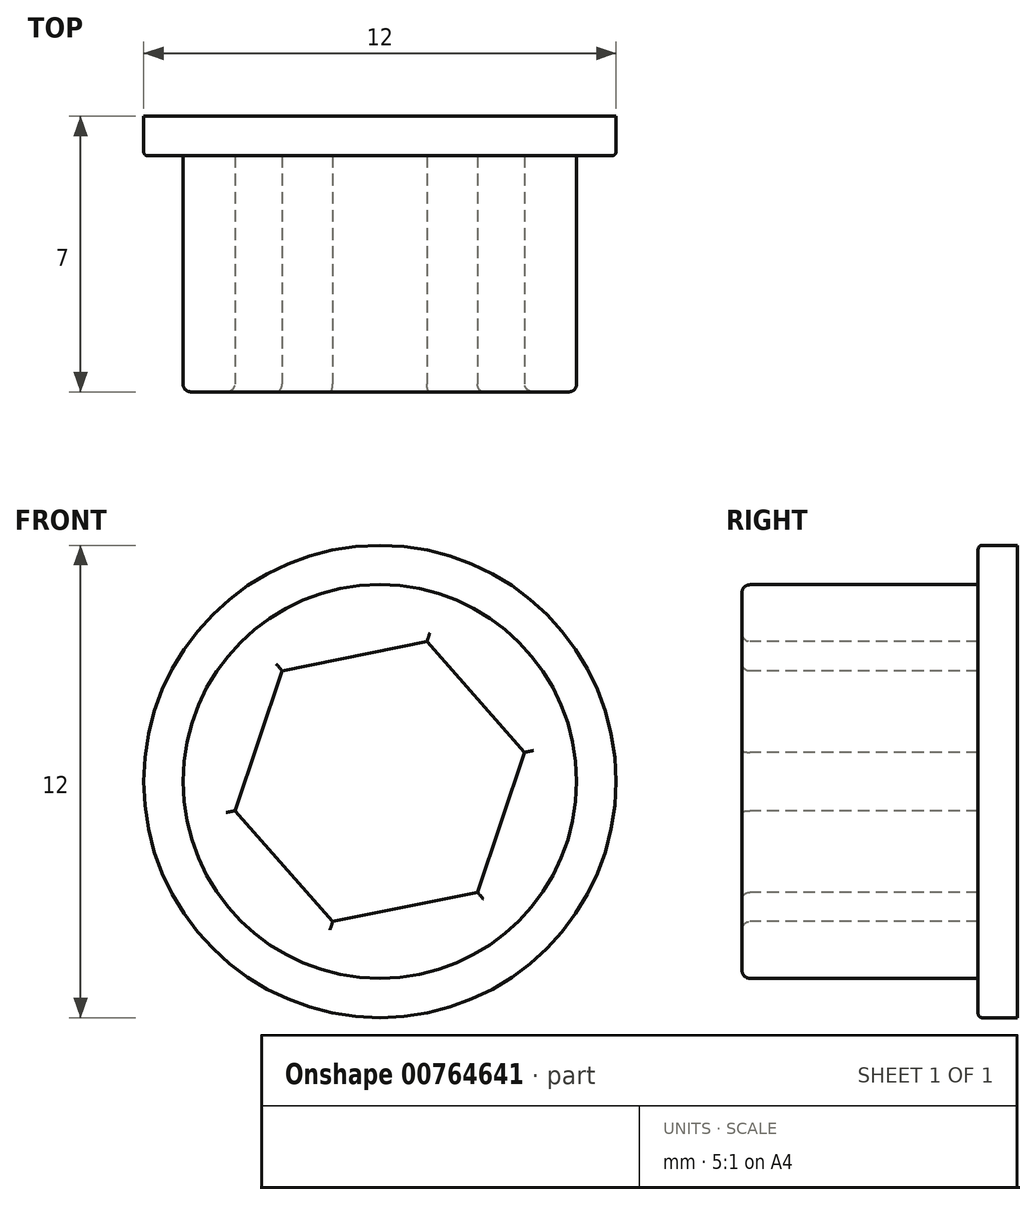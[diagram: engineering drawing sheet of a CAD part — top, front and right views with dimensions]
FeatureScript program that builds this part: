
annotation { "Feature Type Name" : "Feature", "Feature Type Description" : "" }
export const myFeature = defineFeature(function(context is Context, id is Id, definition is map)
    precondition{}
    {
        {
            var Q0;
            Q0=qCreatedBy(makeId("Front.planeOp"),FACE);
            var sketch = newSketch(context, id + "F0", { "sketchPlane" : qUnion([Q0])});
            skCircle(sketch, "E0", {"center": v(0, 0) * mm, "radius": 6 * mm});
            skSolve(sketch);
        }
        {
            var Q0;
            Q0 = qSketchRegion(id + "F0", true);
            extrude(context, id + "F1", {"entities" : qUnion([Q0]), "oppositeDirection" : true, "depth" : 1 * mm, "offsetDistance" : 25 * mm});
        }
        {
            var Q0;
            Q0=makeQuery(id+"F1.opExtrude","CAP_FACE",FACE,{"disambiguationData":[OSD([sQuery(id+"F0.wireOp",EDGE,"E0")])],"isStart":true});
            var sketch = newSketch(context, id + "F2", { "sketchPlane" : qUnion([Q0])});
            skCircle(sketch, "E1", {"center": v(0, 0) * mm, "radius": 5 * mm});
            skSolve(sketch);
        }
        {
            var Q0;
            Q0 = qSketchRegion(id + "F2", true);
            extrude(context, id + "F3", {"entities" : qUnion([Q0]), "operationType" : NewBodyOperationType.ADD, "depth" : 6 * mm, "offsetDistance" : 25 * mm});
        }
        {
            var Q0;
            Q0=makeQuery(id+"F3.opExtrude","CAP_FACE",FACE,{"disambiguationData":[OSD([sQuery(id+"F2.wireOp",EDGE,"E1")])],"isStart":false});
            var sketch = newSketch(context, id + "F4", { "sketchPlane" : qUnion([Q0])});
            skCircle(sketch, "E2.cCircle", {"center": v(0, 0) * mm, "radius": 3.25 * mm, "construction": true});
            skLineSegment(sketch, "E2.0", {"start": v(1.2, 3.56) * mm, "end": v(3.68, 0.74) * mm});
            skLineSegment(sketch, "E2.1", {"start": v(3.68, 0.74) * mm, "end": v(2.48, -2.81) * mm});
            skLineSegment(sketch, "E2.2", {"start": v(2.48, -2.81) * mm, "end": v(-1.2, -3.56) * mm});
            skLineSegment(sketch, "E2.3", {"start": v(-1.2, -3.56) * mm, "end": v(-3.68, -0.74) * mm});
            skLineSegment(sketch, "E2.4", {"start": v(-3.68, -0.74) * mm, "end": v(-2.48, 2.81) * mm});
            skLineSegment(sketch, "E2.5", {"start": v(-2.48, 2.81) * mm, "end": v(1.2, 3.56) * mm});
            skPoint(sketch, "E2.0.midPoint", {"position": v(2.44, 2.15) * mm});
            skSolve(sketch);
        }
        {
            var Q0;
            Q0 = qSketchRegion(id + "F4", true);
            extrude(context, id + "F5", {"entities" : qUnion([Q0]), "operationType" : NewBodyOperationType.REMOVE, "oppositeDirection" : true, "depth" : 6 * mm, "offsetDistance" : 25 * mm});
        }
        {
            var Q0;
            Q0=makeQuery(id+"F3.opExtrude","CAP_FACE",FACE,{"disambiguationData":[OSD([sQuery(id+"F2.wireOp",EDGE,"E1")])],"isStart":false});
            fillet(context, id + "F6", {"entities" : qUnion([Q0]), "radius" : 0.2 * mm, "tangentPropagation" : true, "allowEdgeOverflow" : false});
        }
        {
            var Q0;
            Q0=makeQuery(id+"F1.opExtrude","CAP_EDGE",EDGE,{"disambiguationData":[OSD([sQuery(id+"F0.wireOp",EDGE,"E0")])],"isStart":true});
            fillet(context, id + "F7", {"entities" : qUnion([Q0]), "radius" : 0.1 * mm, "tangentPropagation" : true, "allowEdgeOverflow" : false});
        }
    });
